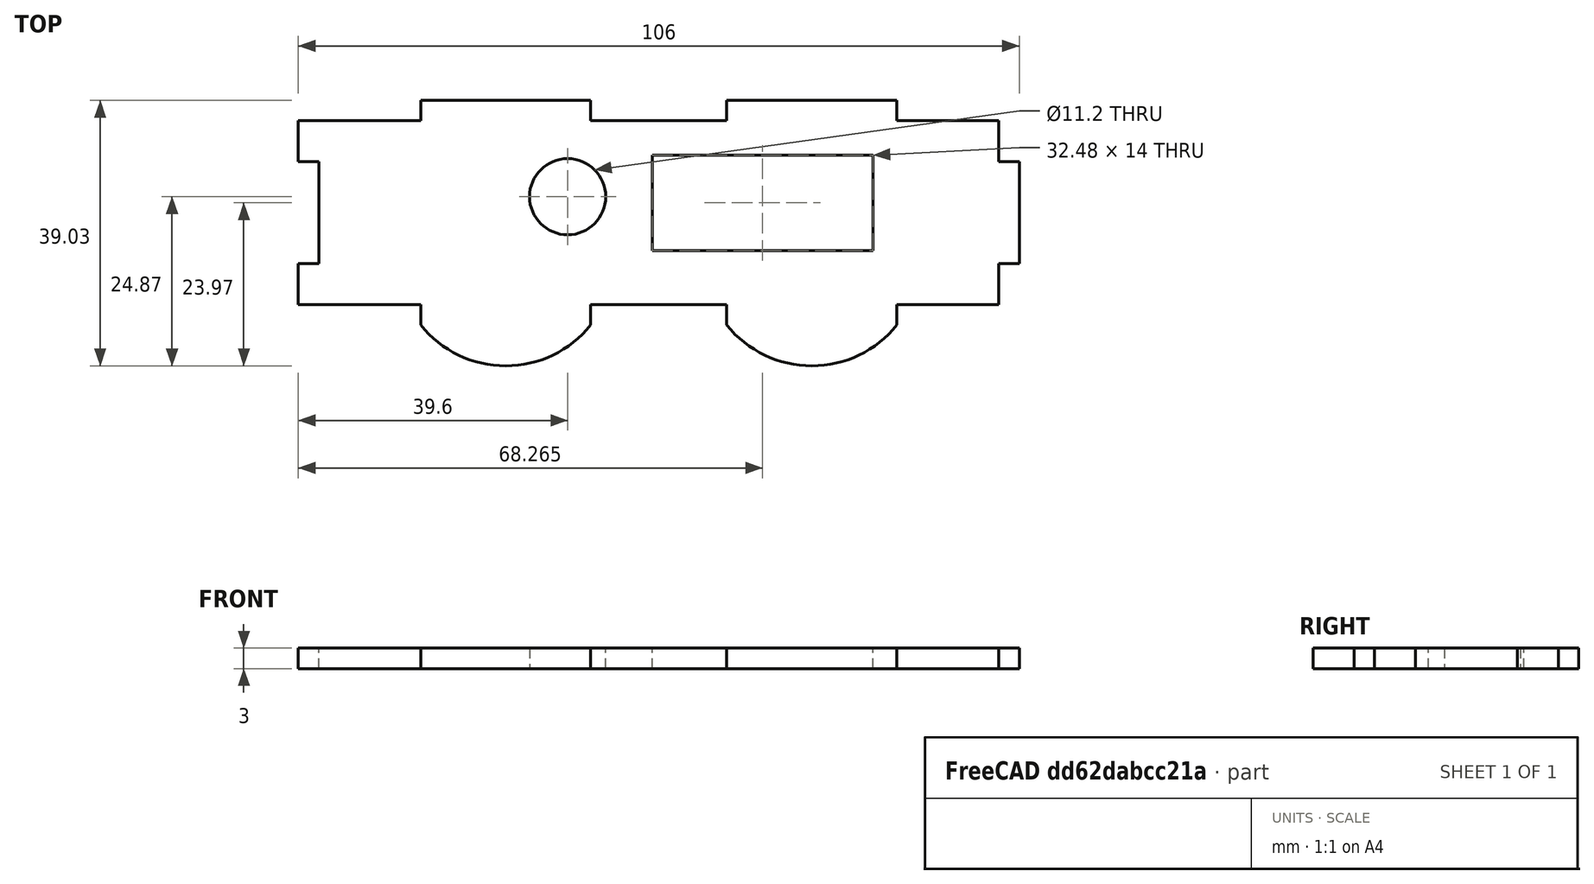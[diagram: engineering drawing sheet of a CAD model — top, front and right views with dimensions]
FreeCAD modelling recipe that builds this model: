
FCSTD DOCUMENT  (FreeCAD 0.19R24267 +99 (Git))
Label: side3
License: All rights reserved
LicenseURL: http://en.wikipedia.org/wiki/All_rights_reserved
objects: App::Part×1, Sketcher::SketchObject×1, Part::Extrusion×1
note: 2 computed .brp shape members not serialized (recipe doc carries the construction recipe); baked Part::Feature solids carry a one-line shape summary decoded from their .brp

FEATURE [App::Part] Part
  Origin = -> Origin
FEATURE [Sketcher::SketchObject] Sketch
  FullyConstrained = false
  sketch-geometry (53):
    g0: LineSegment StartX=0 StartY=0 StartZ=0 EndX=100 EndY=0 EndZ=0
    g1: LineSegment StartX=100 StartY=0 StartZ=0 EndX=100 EndY=1.6 EndZ=0
    g2: LineSegment StartX=100 StartY=1.6 StartZ=0 EndX=0 EndY=1.6 EndZ=0
    g3: LineSegment StartX=0 StartY=1.6 StartZ=0 EndX=0 EndY=0 EndZ=0
    g4: LineSegment StartX=0 StartY=-6.37 StartZ=0 EndX=100 EndY=-6.37 EndZ=0
    g5: LineSegment StartX=100 StartY=-6.37 StartZ=0 EndX=100 EndY=20.66 EndZ=0
    g6: LineSegment StartX=100 StartY=20.66 StartZ=0 EndX=0 EndY=20.66 EndZ=0
    g7: LineSegment StartX=0 StartY=20.66 StartZ=0 EndX=0 EndY=-6.37 EndZ=0
    g8: LineSegment StartX=15 StartY=-6.37 StartZ=0 EndX=40 EndY=-6.37 EndZ=0
    g9: LineSegment StartX=40 StartY=-6.37 StartZ=0 EndX=40 EndY=-9.37 EndZ=0
    g10: LineSegment StartX=40 StartY=-9.37 StartZ=0 EndX=15 EndY=-9.37 EndZ=0
    g11: LineSegment StartX=15 StartY=-9.37 StartZ=0 EndX=15 EndY=-6.37 EndZ=0
    g12: LineSegment StartX=60 StartY=-6.37 StartZ=0 EndX=85 EndY=-6.37 EndZ=0
    g13: LineSegment StartX=85 StartY=-6.37 StartZ=0 EndX=85 EndY=-9.37 EndZ=0
    g14: LineSegment StartX=85 StartY=-9.37 StartZ=0 EndX=60 EndY=-9.37 EndZ=0
    g15: LineSegment StartX=60 StartY=-9.37 StartZ=0 EndX=60 EndY=-6.37 EndZ=0
    g16: LineSegment StartX=15 StartY=20.66 StartZ=0 EndX=40 EndY=20.66 EndZ=0
    g17: LineSegment StartX=40 StartY=20.66 StartZ=0 EndX=40 EndY=23.66 EndZ=0
    g18: LineSegment StartX=40 StartY=23.66 StartZ=0 EndX=15 EndY=23.66 EndZ=0
    g19: LineSegment StartX=15 StartY=23.66 StartZ=0 EndX=15 EndY=20.66 EndZ=0
    g20: LineSegment StartX=60 StartY=20.66 StartZ=0 EndX=85 EndY=20.66 EndZ=0
    g21: LineSegment StartX=85 StartY=20.66 StartZ=0 EndX=85 EndY=23.66 EndZ=0
    g22: LineSegment StartX=85 StartY=23.66 StartZ=0 EndX=60 EndY=23.66 EndZ=0
    g23: LineSegment StartX=60 StartY=23.66 StartZ=0 EndX=60 EndY=20.66 EndZ=0
    g24: LineSegment StartX=100 StartY=14.66 StartZ=0 EndX=103 EndY=14.66 EndZ=0
    g25: LineSegment StartX=103 StartY=14.66 StartZ=0 EndX=103 EndY=-0.34 EndZ=0
    g26: LineSegment StartX=103 StartY=-0.34 StartZ=0 EndX=100 EndY=-0.34 EndZ=0
    g27: LineSegment StartX=100 StartY=-0.34 StartZ=0 EndX=100 EndY=14.66 EndZ=0
    g28: LineSegment StartX=0 StartY=-0.34 StartZ=0 EndX=0 EndY=14.66 EndZ=0
    g29: LineSegment StartX=0 StartY=20.66 StartZ=0 EndX=15 EndY=20.66 EndZ=0
    g30: LineSegment StartX=40 StartY=20.66 StartZ=0 EndX=60 EndY=20.66 EndZ=0
    g31: LineSegment StartX=85 StartY=20.66 StartZ=0 EndX=100 EndY=20.66 EndZ=0
    g32: LineSegment StartX=100 StartY=-0.34 StartZ=0 EndX=100 EndY=-6.37 EndZ=0
    g33: LineSegment StartX=100 StartY=-6.37 StartZ=0 EndX=85 EndY=-6.37 EndZ=0
    g34: LineSegment StartX=60 StartY=-6.37 StartZ=0 EndX=40 EndY=-6.37 EndZ=0
    g35: LineSegment StartX=15 StartY=-6.37 StartZ=0 EndX=0 EndY=-6.37 EndZ=0
    g36: LineSegment StartX=100 StartY=20.66 StartZ=0 EndX=100 EndY=14.66 EndZ=0
    g37: ArcOfCircle CenterX=27.5 CenterY=0.650833 CenterZ=0 NormalX=0 NormalY=0 NormalZ=1 AngleXU=0 Radius=16.0208 StartAngle=3.81735 EndAngle=5.60743
    g38: GeomPoint X=27.5 Y=-15.37 Z=0
    g39: ArcOfCircle CenterX=72.5 CenterY=0.650833 CenterZ=0 NormalX=0 NormalY=0 NormalZ=1 AngleXU=0 Radius=16.0208 StartAngle=3.81735 EndAngle=5.60743
    g40: GeomPoint X=72.5 Y=-15.37 Z=0
    g41: LineSegment StartX=0 StartY=14.66 StartZ=0 EndX=-3 EndY=14.66 EndZ=0
    g42: LineSegment StartX=-3 StartY=-0.34 StartZ=0 EndX=0 EndY=-0.34 EndZ=0
    g43: LineSegment StartX=-3 StartY=-0.34 StartZ=0 EndX=-3 EndY=-6.37 EndZ=0
    g44: LineSegment StartX=-3 StartY=-6.37 StartZ=0 EndX=0 EndY=-6.37 EndZ=0
    g45: LineSegment StartX=-3 StartY=14.66 StartZ=0 EndX=-3 EndY=20.66 EndZ=0
    g46: LineSegment StartX=-3 StartY=20.66 StartZ=0 EndX=0 EndY=20.66 EndZ=0
    g47: LineSegment StartX=0 StartY=14.66 StartZ=0 EndX=0 EndY=-0.34 EndZ=0
    g48: Circle CenterX=36.6 CenterY=9.5 CenterZ=0 NormalX=0 NormalY=0 NormalZ=1 AngleXU=0 Radius=5.6
    g49: LineSegment StartX=49.025 StartY=1.6 StartZ=0 EndX=81.505 EndY=1.6 EndZ=0
    g50: LineSegment StartX=81.505 StartY=1.6 StartZ=0 EndX=81.505 EndY=15.6 EndZ=0
    g51: LineSegment StartX=81.505 StartY=15.6 StartZ=0 EndX=49.025 EndY=15.6 EndZ=0
    g52: LineSegment StartX=49.025 StartY=15.6 StartZ=0 EndX=49.025 EndY=1.6 EndZ=0
  constraints (144):
    c: Coincident(g0,g1)
    c: Coincident(g1,g2)
    c: Coincident(g2,g3)
    c: Coincident(g3,g0)
    c: Horizontal(g0)
    c: Horizontal(g2)
    c: Vertical(g1)
    c: Vertical(g3)
    c: Coincident(g0,g-1)
    c: DistanceX(g2,g2) = 100
    c: DistanceY(g3,g3) = 1.6
    c: Coincident(g4,g5)
    c: Coincident(g5,g6)
    c: Coincident(g6,g7)
    c: Coincident(g7,g4)
    c: Horizontal(g4)
    c: Horizontal(g6)
    c: Vertical(g5)
    c: Vertical(g7)
    c: PointOnObject(g4,g-2)
    c: Equal(g6,g2)
    c: DistanceY(g2,g6) = 19.06
    c: DistanceY(g4,g-1) = 6.37
    c: Coincident(g8,g9)
    c: Coincident(g9,g10)
    c: Coincident(g10,g11)
    c: Coincident(g11,g8)
    c: Horizontal(g8)
    c: Horizontal(g10)
    c: Vertical(g9)
    c: Vertical(g11)
    c: PointOnObject(g8,g4)
    c: Coincident(g12,g13)
    c: Coincident(g13,g14)
    c: Coincident(g14,g15)
    c: Coincident(g15,g12)
    c: Horizontal(g12)
    c: Horizontal(g14)
    c: Vertical(g13)
    c: Vertical(g15)
    c: PointOnObject(g12,g4)
    c: Coincident(g16,g17)
    c: Coincident(g17,g18)
    c: Coincident(g18,g19)
    c: Coincident(g19,g16)
    c: Horizontal(g16)
    c: Horizontal(g18)
    c: Vertical(g17)
    c: Vertical(g19)
    c: PointOnObject(g16,g6)
    c: Coincident(g20,g21)
    c: Coincident(g21,g22)
    c: Coincident(g22,g23)
    c: Coincident(g23,g20)
    c: Horizontal(g20)
    c: Horizontal(g22)
    c: Vertical(g21)
    c: Vertical(g23)
    c: PointOnObject(g20,g6)
    c: Coincident(g24,g25)
    c: Coincident(g25,g26)
    c: Coincident(g26,g27)
    c: Coincident(g27,g24)
    c: Horizontal(g24)
    c: Horizontal(g26)
    c: Vertical(g25)
    c: Vertical(g27)
    c: PointOnObject(g24,g5)
    c: Vertical(g28)
    c: PointOnObject(g28,g7)
    c: Equal(g18,g22)
    c: Equal(g14,g10)
    c: DistanceX(g18,g18) = 25
    c: Equal(g11,g15)
    c: Equal(g15,g23)
    c: Equal(g23,g24)
    c: DistanceY(g23,g23) = 3
    c: DistanceX(g6,g18) = 15
    c: DistanceX(g21,g5) = 15
    c: DistanceX(g13,g4) = 15
    c: DistanceX(g4,g10) = 15
    c: Equal(g14,g22)
    c: DistanceY(g25,g25) = 15
    c: DistanceY(g24,g5) = 6
    c: Coincident(g29,g16)
    c: Coincident(g30,g16)
    c: Coincident(g30,g20)
    c: Coincident(g31,g20)
    c: Coincident(g31,g5)
    c: Coincident(g32,g26)
    c: Coincident(g32,g4)
    c: Coincident(g33,g32)
    c: Coincident(g33,g12)
    c: Coincident(g34,g12)
    c: Coincident(g34,g8)
    c: Coincident(g35,g8)
    c: Coincident(g35,g4)
    c: Coincident(g36,g31)
    c: Coincident(g36,g24)
    c: Coincident(g37,g9)
    c: Coincident(g37,g10)
    c: PointOnObject(g38,g37)
    c: DistanceY(g38,g9) = 6
    c: DistanceX(g38,g9) = 12.5
    c: Coincident(g39,g14)
    c: Coincident(g39,g13)
    c: PointOnObject(g40,g39)
    c: DistanceX(g40,g13) = 12.5
    c: DistanceY(g40,g13) = 6
    c: Coincident(g41,g28)
    c: Horizontal(g41)
    c: PointOnObject(g42,g7)
    c: Horizontal(g42)
    c: DistanceY(g42,g41) = 15
    c: DistanceX(g41,g41) = 3
    c: Horizontal(g41,g24)
    c: Vertical(g43)
    c: Coincident(g44,g43)
    c: Coincident(g44,g35)
    c: Horizontal(g44)
    c: Coincident(g45,g41)
    c: Vertical(g45)
    c: Coincident(g46,g29)
    c: Horizontal(g46)
    c: Horizontal(g29,g19)
    c: Coincident(g47,g41)
    c: Coincident(g47,g42)
    c: DistanceY(g45,g45) = 6
    c: Equal(g43,g32)
    c: DistanceY(g2,g48) = 7.9
    c: Radius(g48) = 5.6
    c: DistanceX(g-1,g48) = 36.6
    c: Coincident(g49,g50)
    c: Coincident(g50,g51)
    c: Coincident(g51,g52)
    c: Coincident(g52,g49)
    c: Horizontal(g49)
    c: Horizontal(g51)
    c: Vertical(g50)
    c: Vertical(g52)
    c: PointOnObject(g49,g2)
    c: DistanceX(g51,g51) = 32.48
    c: DistanceY(g50,g50) = 14
    c: DistanceX(g-1,g51) = 49.025
FEATURE [Part::Extrusion] Extrude
  Base = -> Sketch
  Dir = (0,0,1)
  DirMode = 2
  FaceMakerClass = Part::FaceMakerBullseye
  LengthFwd = 3
  LengthRev = 0
  Solid = true
  Symmetric = false
